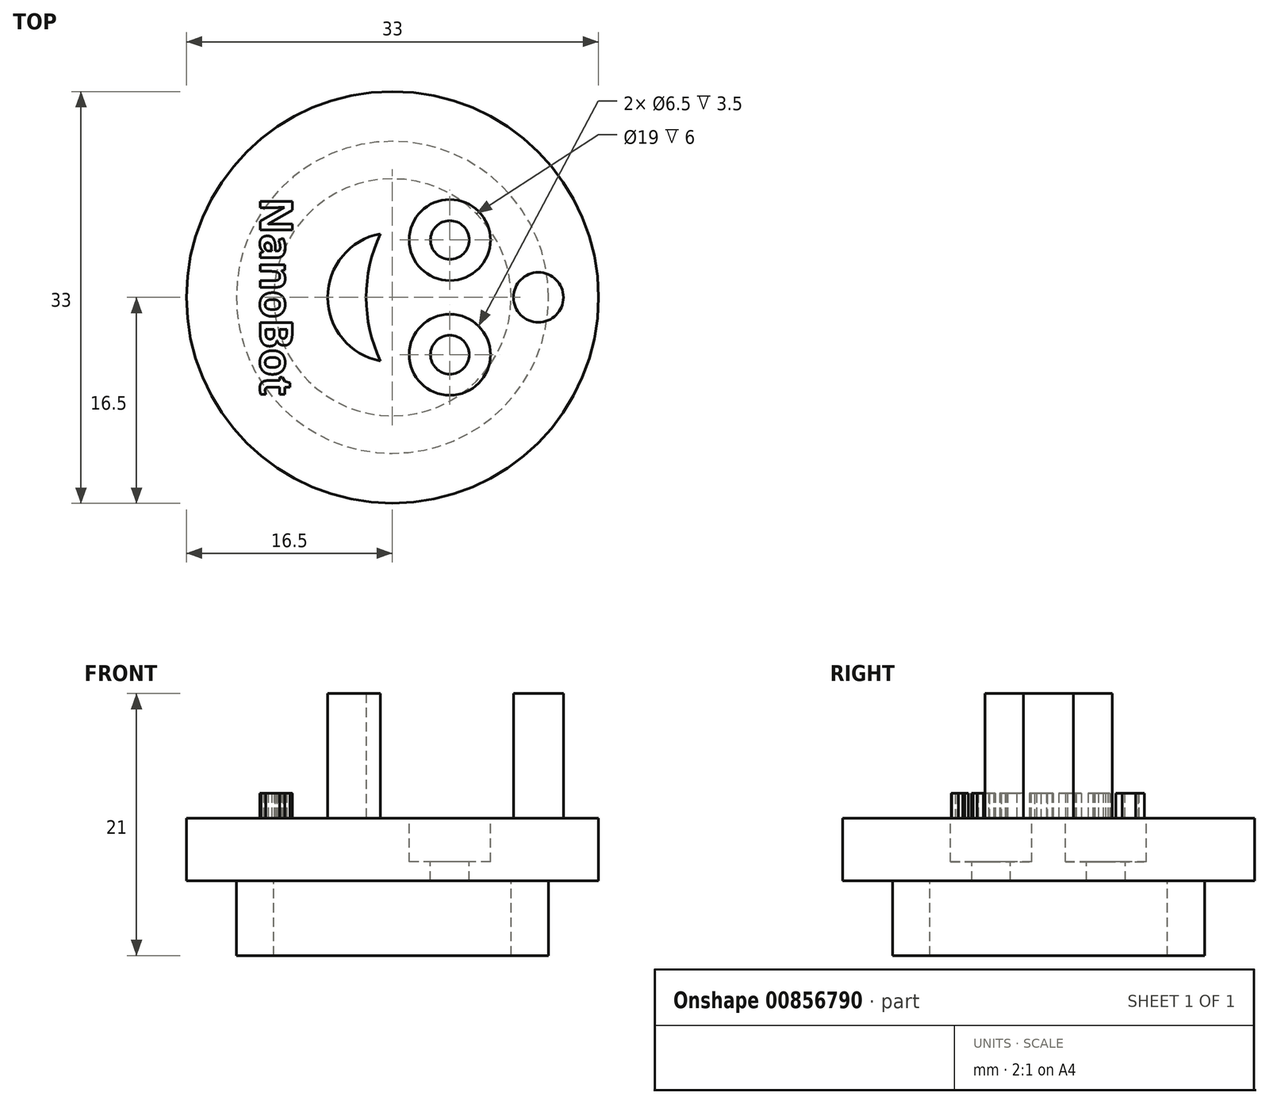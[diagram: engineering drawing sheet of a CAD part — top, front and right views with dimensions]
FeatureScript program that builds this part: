
annotation { "Feature Type Name" : "Feature", "Feature Type Description" : "" }
export const myFeature = defineFeature(function(context is Context, id is Id, definition is map)
    precondition{}
    {
        {
            var Q0;
            Q0=qCreatedBy(makeId("Top.planeOp"),FACE);
            var sketch = newSketch(context, id + "F0", { "sketchPlane" : qUnion([Q0])});
            skCircle(sketch, "E0", {"center": v(0, 0) * mm, "radius": 11.7 * mm});
            skCircle(sketch, "E1", {"center": v(0, 0) * mm, "radius": 16.5 * mm});
            skCircle(sketch, "E2", {"center": v(0, 0) * mm, "radius": 5.2 * mm});
            skLineSegment(sketch, "E3", {"start": v(-0.96, 5.1) * mm, "end": v(-0.96, -5.1) * mm});
            skArc(sketch, "E4", {"start": v(-0.96, 5.1) * mm, "mid": v(-2.1, 0) * mm, "end": v(-0.96, -5.1) * mm});
            skCircle(sketch, "E5", {"center": v(11.7, 0) * mm, "radius": 2 * mm});
            skLineSegment(sketch, "E6", {"start": v(0, 0) * mm, "end": v(8.27, -8.27) * mm, "construction": true});
            skLineSegment(sketch, "E7", {"start": v(0, 0) * mm, "end": v(8.27, 8.27) * mm, "construction": true});
            skCircle(sketch, "E8", {"center": v(4.6, -4.6) * mm, "radius": 1.55 * mm});
            skCircle(sketch, "E9", {"center": v(4.6, 4.6) * mm, "radius": 1.55 * mm});
            skCircle(sketch, "E10", {"center": v(4.6, -4.6) * mm, "radius": 3.25 * mm});
            skCircle(sketch, "E11", {"center": v(4.6, 4.6) * mm, "radius": 3.25 * mm});
            skSolve(sketch);
        }
        {
            var Q0;
            {var subQ0=sQuery(id+"F0.wireOp",EDGE,"ffSkBEEl-9YDE-j9nG-bAPr-YQZfFxrPOlck");var subQ1=sQuery(id+"F0.wireOp",EDGE,"E0");var subQ2=makeQuery(id+"F0.imprint","INTERSECT",VERTEX,{"disambiguationData":[OD(0.0)],"derivedFrom":[subQ1,subQ0]});Q0=makeQuery(id+"F0.imprint","IMPRINT",FACE,{"disambiguationData":[TD([[makeQuery(id+"F0.imprint","IMPRINT",EDGE,{"disambiguationData":[TD([[subQ2,-1.0]])],"derivedFrom":subQ1}),1.0]])]});}
            var Q1;
            {var subQ0=sQuery(id+"F0.wireOp",EDGE,"ffSkBEEl-9YDE-j9nG-bAPr-YQZfFxrPOlck");var subQ1=sQuery(id+"F0.wireOp",EDGE,"E0");var subQ2=makeQuery(id+"F0.imprint","INTERSECT",VERTEX,{"disambiguationData":[OD(0.0)],"derivedFrom":[subQ1,subQ0]});Q1=makeQuery(id+"F0.imprint","IMPRINT",FACE,{"disambiguationData":[TD([[makeQuery(id+"F0.imprint","IMPRINT",EDGE,{"disambiguationData":[TD([[subQ2,1.0]])],"derivedFrom":subQ1}),1.0]])]});}
            var Q2;
            {var subQ0=sQuery(id+"F0.wireOp",EDGE,"ffSkBEEl-9YDE-j9nG-bAPr-YQZfFxrPOlck");var subQ1=sQuery(id+"F0.wireOp",EDGE,"E0");var subQ2=makeQuery(id+"F0.imprint","INTERSECT",VERTEX,{"disambiguationData":[OD(0.0)],"derivedFrom":[subQ1,subQ0]});Q2=makeQuery(id+"F0.imprint","IMPRINT",FACE,{"disambiguationData":[TD([[makeQuery(id+"F0.imprint","IMPRINT",EDGE,{"disambiguationData":[TD([[subQ2,1.0]])],"derivedFrom":subQ1}),-1.0]])]});}
            var Q3;
            Q3=makeQuery(id+"F0.imprint","IMPRINT",FACE,{"disambiguationData":[TD([[makeQuery(id+"F0.imprint","IMPRINT",EDGE,{"derivedFrom":sQuery(id+"F0.wireOp",EDGE,"E1")}),1.0]])]});
            var Q4;
            Q4=makeQuery(id+"F0.imprint","IMPRINT",FACE,{"disambiguationData":[TD([[makeQuery(id+"F0.imprint","IMPRINT",EDGE,{"derivedFrom":sQuery(id+"F0.wireOp",EDGE,"E3")}),-1.0]])]});
            var Q5;
            {var subQ0=sQuery(id+"F0.wireOp",EDGE,"E4");Q5=makeQuery(id+"F0.imprint","IMPRINT",FACE,{"disambiguationData":[TD([[makeQuery(id+"F0.imprint","IMPRINT",EDGE,{"derivedFrom":subQ0}),-1.0]])]});}
            var Q6;
            {var subQ1=sQuery(id+"F0.wireOp",EDGE,"E3");Q6=makeQuery(id+"F0.imprint","IMPRINT",FACE,{"disambiguationData":[TD([[makeQuery(id+"F0.imprint","IMPRINT",EDGE,{"derivedFrom":subQ1}),1.0]])]});}
            var Q7;
            {var subQ0=sQuery(id+"F0.wireOp",EDGE,"E5");var subQ1=sQuery(id+"F0.wireOp",EDGE,"E0");var subQ2=makeQuery(id+"F0.imprint","INTERSECT",VERTEX,{"disambiguationData":[OD(0.0)],"derivedFrom":[subQ1,subQ0]});Q7=makeQuery(id+"F0.imprint","IMPRINT",FACE,{"disambiguationData":[TD([[makeQuery(id+"F0.imprint","IMPRINT",EDGE,{"disambiguationData":[TD([[subQ2,-1.0]])],"derivedFrom":subQ1}),-1.0]])]});}
            var Q8;
            {var subQ0=sQuery(id+"F0.wireOp",EDGE,"E10");var subQ1=sQuery(id+"F0.wireOp",EDGE,"E2");var subQ2=makeQuery(id+"F0.imprint","INTERSECT",VERTEX,{"disambiguationData":[OD(0.0)],"derivedFrom":[subQ1,subQ0]});Q8=makeQuery(id+"F0.imprint","IMPRINT",FACE,{"disambiguationData":[TD([[makeQuery(id+"F0.imprint","IMPRINT",EDGE,{"disambiguationData":[TD([[subQ2,-1.0]])],"derivedFrom":subQ1}),-1.0]])]});}
            var Q9;
            {var subQ0=sQuery(id+"F0.wireOp",EDGE,"E10");var subQ1=sQuery(id+"F0.wireOp",EDGE,"E2");var subQ2=makeQuery(id+"F0.imprint","INTERSECT",VERTEX,{"disambiguationData":[OD(0.0)],"derivedFrom":[subQ1,subQ0]});Q9=makeQuery(id+"F0.imprint","IMPRINT",FACE,{"disambiguationData":[TD([[makeQuery(id+"F0.imprint","IMPRINT",EDGE,{"disambiguationData":[TD([[subQ2,-1.0]])],"derivedFrom":subQ1}),1.0]])]});}
            var Q10;
            {var subQ0=sQuery(id+"F0.wireOp",EDGE,"E9");var subQ1=sQuery(id+"F0.wireOp",EDGE,"E2");var subQ2=makeQuery(id+"F0.imprint","INTERSECT",VERTEX,{"disambiguationData":[OD(0.0)],"derivedFrom":[subQ1,subQ0]});Q10=makeQuery(id+"F0.imprint","IMPRINT",FACE,{"disambiguationData":[TD([[makeQuery(id+"F0.imprint","IMPRINT",EDGE,{"disambiguationData":[TD([[subQ2,1.0]])],"derivedFrom":subQ1}),1.0]])]});}
            var Q11;
            {var subQ0=sQuery(id+"F0.wireOp",EDGE,"E9");var subQ1=sQuery(id+"F0.wireOp",EDGE,"E2");var subQ2=makeQuery(id+"F0.imprint","INTERSECT",VERTEX,{"disambiguationData":[OD(0.0)],"derivedFrom":[subQ1,subQ0]});Q11=makeQuery(id+"F0.imprint","IMPRINT",FACE,{"disambiguationData":[TD([[makeQuery(id+"F0.imprint","IMPRINT",EDGE,{"disambiguationData":[TD([[subQ2,1.0]])],"derivedFrom":subQ1}),-1.0]])]});}
            extrude(context, id + "F1", {"entities" : qUnion([Q0, Q1, Q2, Q3, Q4, Q5, Q6, Q7, Q8, Q9, Q10, Q11]), "oppositeDirection" : true, "depth" : 5 * mm, "offsetDistance" : 25 * mm});
        }
        {
            var Q0;
            {var subQ0=sQuery(id+"F0.wireOp",EDGE,"E5");var subQ1=sQuery(id+"F0.wireOp",EDGE,"E0");var subQ2=makeQuery(id+"F0.imprint","INTERSECT",VERTEX,{"disambiguationData":[OD(0.0)],"derivedFrom":[subQ1,subQ0]});Q0=makeQuery(id+"F0.imprint","IMPRINT",FACE,{"disambiguationData":[TD([[makeQuery(id+"F0.imprint","IMPRINT",EDGE,{"disambiguationData":[TD([[subQ2,-1.0]])],"derivedFrom":subQ1}),-1.0]])]});}
            var Q1;
            {var subQ0=sQuery(id+"F0.wireOp",EDGE,"E5");var subQ1=sQuery(id+"F0.wireOp",EDGE,"E0");var subQ2=makeQuery(id+"F0.imprint","INTERSECT",VERTEX,{"disambiguationData":[OD(0.0)],"derivedFrom":[subQ1,subQ0]});Q1=makeQuery(id+"F0.imprint","IMPRINT",FACE,{"disambiguationData":[TD([[makeQuery(id+"F0.imprint","IMPRINT",EDGE,{"disambiguationData":[TD([[subQ2,-1.0]])],"derivedFrom":subQ1}),1.0]])]});}
            var Q2;
            {var subQ0=sQuery(id+"F0.wireOp",EDGE,"E4");Q2=makeQuery(id+"F0.imprint","IMPRINT",FACE,{"disambiguationData":[TD([[makeQuery(id+"F0.imprint","IMPRINT",EDGE,{"derivedFrom":subQ0}),-1.0]])]});}
            extrude(context, id + "F2", {"entities" : qUnion([Q0, Q1, Q2]), "operationType" : NewBodyOperationType.ADD, "depth" : 10 * mm, "offsetDistance" : 25 * mm});
        }
        {
            var Q0;
            Q0=makeQuery(id+"F1.opExtrude","CAP_FACE",FACE,{"disambiguationData":[OSD([sQuery(id+"F0.wireOp",EDGE,"E1")])],"isStart":false});
            var sketch = newSketch(context, id + "F3", { "sketchPlane" : qUnion([Q0])});
            skCircle(sketch, "E12", {"center": v(0, 0) * mm, "radius": 12.5 * mm});
            skCircle(sketch, "E13", {"center": v(0, 0) * mm, "radius": 9.5 * mm});
            skSolve(sketch);
        }
        {
            var Q0;
            Q0=makeQuery(id+"F3.imprint","IMPRINT",FACE,{"disambiguationData":[TD([[makeQuery(id+"F3.imprint","IMPRINT",EDGE,{"derivedFrom":sQuery(id+"F3.wireOp",EDGE,"E12")}),1.0]])]});
            extrude(context, id + "F4", {"entities" : qUnion([Q0]), "operationType" : NewBodyOperationType.ADD, "depth" : 6 * mm, "offsetDistance" : 25 * mm});
        }
        {
            var Q0;
            {var subQ0=sQuery(id+"F0.wireOp",EDGE,"E10");var subQ1=sQuery(id+"F0.wireOp",EDGE,"E2");var subQ2=makeQuery(id+"F0.imprint","INTERSECT",VERTEX,{"disambiguationData":[OD(0.0)],"derivedFrom":[subQ1,subQ0]});Q0=makeQuery(id+"F0.imprint","IMPRINT",FACE,{"disambiguationData":[TD([[makeQuery(id+"F0.imprint","IMPRINT",EDGE,{"disambiguationData":[TD([[subQ2,-1.0]])],"derivedFrom":subQ1}),-1.0]])]});}
            var Q1;
            {var subQ0=sQuery(id+"F0.wireOp",EDGE,"E10");var subQ1=sQuery(id+"F0.wireOp",EDGE,"E2");var subQ2=makeQuery(id+"F0.imprint","INTERSECT",VERTEX,{"disambiguationData":[OD(0.0)],"derivedFrom":[subQ1,subQ0]});Q1=makeQuery(id+"F0.imprint","IMPRINT",FACE,{"disambiguationData":[TD([[makeQuery(id+"F0.imprint","IMPRINT",EDGE,{"disambiguationData":[TD([[subQ2,-1.0]])],"derivedFrom":subQ1}),1.0]])]});}
            var Q2;
            {var subQ0=sQuery(id+"F0.wireOp",EDGE,"E8");var subQ1=sQuery(id+"F0.wireOp",EDGE,"E2");var subQ2=makeQuery(id+"F0.imprint","INTERSECT",VERTEX,{"disambiguationData":[OD(0.0)],"derivedFrom":[subQ1,subQ0]});Q2=makeQuery(id+"F0.imprint","IMPRINT",FACE,{"disambiguationData":[TD([[makeQuery(id+"F0.imprint","IMPRINT",EDGE,{"disambiguationData":[TD([[subQ2,-1.0]])],"derivedFrom":subQ1}),1.0]])]});}
            var Q3;
            {var subQ0=sQuery(id+"F0.wireOp",EDGE,"E9");var subQ1=sQuery(id+"F0.wireOp",EDGE,"E2");var subQ2=makeQuery(id+"F0.imprint","INTERSECT",VERTEX,{"disambiguationData":[OD(0.0)],"derivedFrom":[subQ1,subQ0]});Q3=makeQuery(id+"F0.imprint","IMPRINT",FACE,{"disambiguationData":[TD([[makeQuery(id+"F0.imprint","IMPRINT",EDGE,{"disambiguationData":[TD([[subQ2,1.0]])],"derivedFrom":subQ1}),-1.0]])]});}
            var Q4;
            {var subQ0=sQuery(id+"F0.wireOp",EDGE,"E9");var subQ1=sQuery(id+"F0.wireOp",EDGE,"E2");var subQ2=makeQuery(id+"F0.imprint","INTERSECT",VERTEX,{"disambiguationData":[OD(0.0)],"derivedFrom":[subQ1,subQ0]});Q4=makeQuery(id+"F0.imprint","IMPRINT",FACE,{"disambiguationData":[TD([[makeQuery(id+"F0.imprint","IMPRINT",EDGE,{"disambiguationData":[TD([[subQ2,1.0]])],"derivedFrom":subQ1}),1.0]])]});}
            var Q5;
            {var subQ0=sQuery(id+"F0.wireOp",EDGE,"E9");var subQ1=sQuery(id+"F0.wireOp",EDGE,"E2");var subQ2=makeQuery(id+"F0.imprint","INTERSECT",VERTEX,{"disambiguationData":[OD(0.0)],"derivedFrom":[subQ1,subQ0]});Q5=makeQuery(id+"F0.imprint","IMPRINT",FACE,{"disambiguationData":[TD([[makeQuery(id+"F0.imprint","IMPRINT",EDGE,{"disambiguationData":[TD([[subQ2,-1.0]])],"derivedFrom":subQ1}),1.0]])]});}
            extrude(context, id + "F5", {"entities" : qUnion([Q0, Q1, Q2, Q3, Q4, Q5]), "operationType" : NewBodyOperationType.REMOVE, "oppositeDirection" : true, "depth" : 3.5 * mm, "offsetDistance" : 25 * mm});
        }
        {
            var Q0;
            Q0=makeQuery(id+"F1.opExtrude","CAP_FACE",FACE,{"disambiguationData":[OSD([sQuery(id+"F0.wireOp",EDGE,"E1"),sQuery(id+"F0.wireOp",EDGE,"E8"),sQuery(id+"F0.wireOp",EDGE,"E9")])],"isStart":true});
            var sketch = newSketch(context, id + "F6", { "sketchPlane" : qUnion([Q0])});
            skText(sketch, "E14", { "text": "NanoBot", "fontName": "OpenSans-Bold.ttf"});
            const initialGuessF6  = {"E14": [-0.01059, 0.008, 0, -1, 0.00259]};
            skSetInitialGuess(sketch, initialGuessF6);
            skSolve(sketch);
        }
        {
            var Q0;
            Q0 = qSketchRegion(id + "F6", true);
            extrude(context, id + "F7", {"entities" : qUnion([Q0]), "operationType" : NewBodyOperationType.ADD, "depth" : 2 * mm, "offsetDistance" : 25 * mm});
        }
    });
